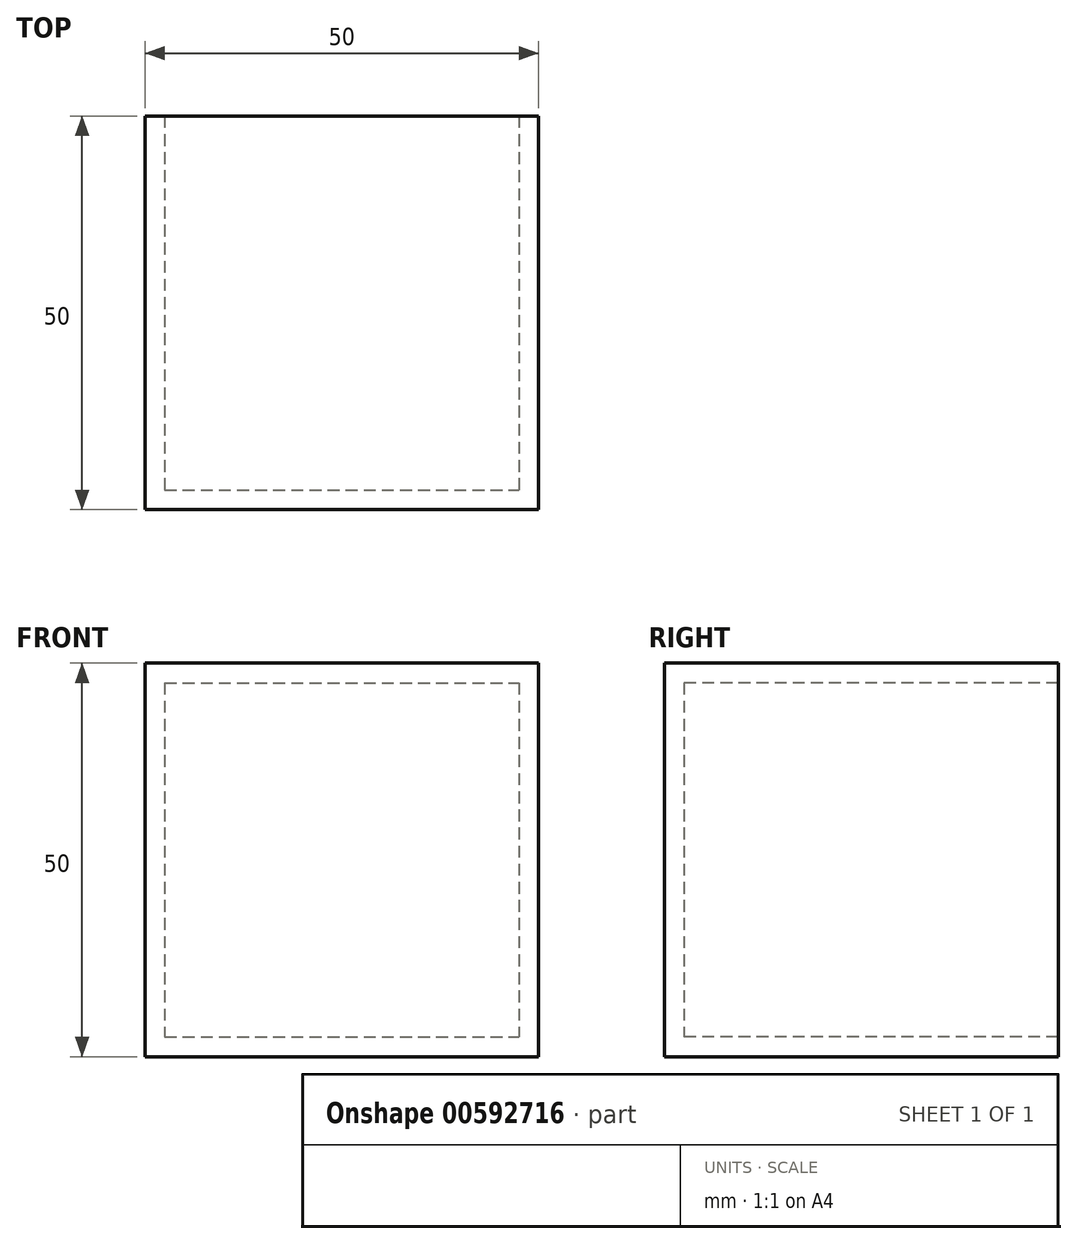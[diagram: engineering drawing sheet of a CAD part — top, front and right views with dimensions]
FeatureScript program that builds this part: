
annotation { "Feature Type Name" : "Feature", "Feature Type Description" : "" }
export const myFeature = defineFeature(function(context is Context, id is Id, definition is map)
    precondition{}
    {
        {
            var Q0;
            Q0=qCreatedBy(makeId("Top.planeOp"),FACE);
            var sketch = newSketch(context, id + "F0", { "sketchPlane" : qUnion([Q0])});
            skLineSegment(sketch, "E0.bottom", {"start": v(-71.67, 59.2) * mm, "end": v(-21.67, 59.2) * mm});
            skLineSegment(sketch, "E0.top", {"start": v(-71.67, 9.2) * mm, "end": v(-21.67, 9.2) * mm});
            skLineSegment(sketch, "E0.left", {"start": v(-71.67, 59.2) * mm, "end": v(-71.67, 9.2) * mm});
            skLineSegment(sketch, "E0.right", {"start": v(-21.67, 59.2) * mm, "end": v(-21.67, 9.2) * mm});
            skSolve(sketch);
        }
        {
            var Q0;
            Q0=makeQuery(id+"F0.imprint","IMPRINT",FACE,{"disambiguationData":[TD([[makeQuery(id+"F0.imprint","IMPRINT",EDGE,{"derivedFrom":sQuery(id+"F0.wireOp",EDGE,"E0.bottom")}),-1.0]])]});
            extrude(context, id + "F1", {"entities" : qUnion([Q0]), "depth" : 50 * mm, "offsetDistance" : 25 * mm});
        }
        {
            var Q0;
            Q0=makeQuery(id+"F1.opExtrude","SWEPT_FACE",FACE,{"disambiguationData":[OSD([sQuery(id+"F0.wireOp",EDGE,"E0.bottom")])]});
            shell(context, id + "F2", {"entities" : qUnion([Q0]), "thickness" : 2.5 * mm});
        }
    });
